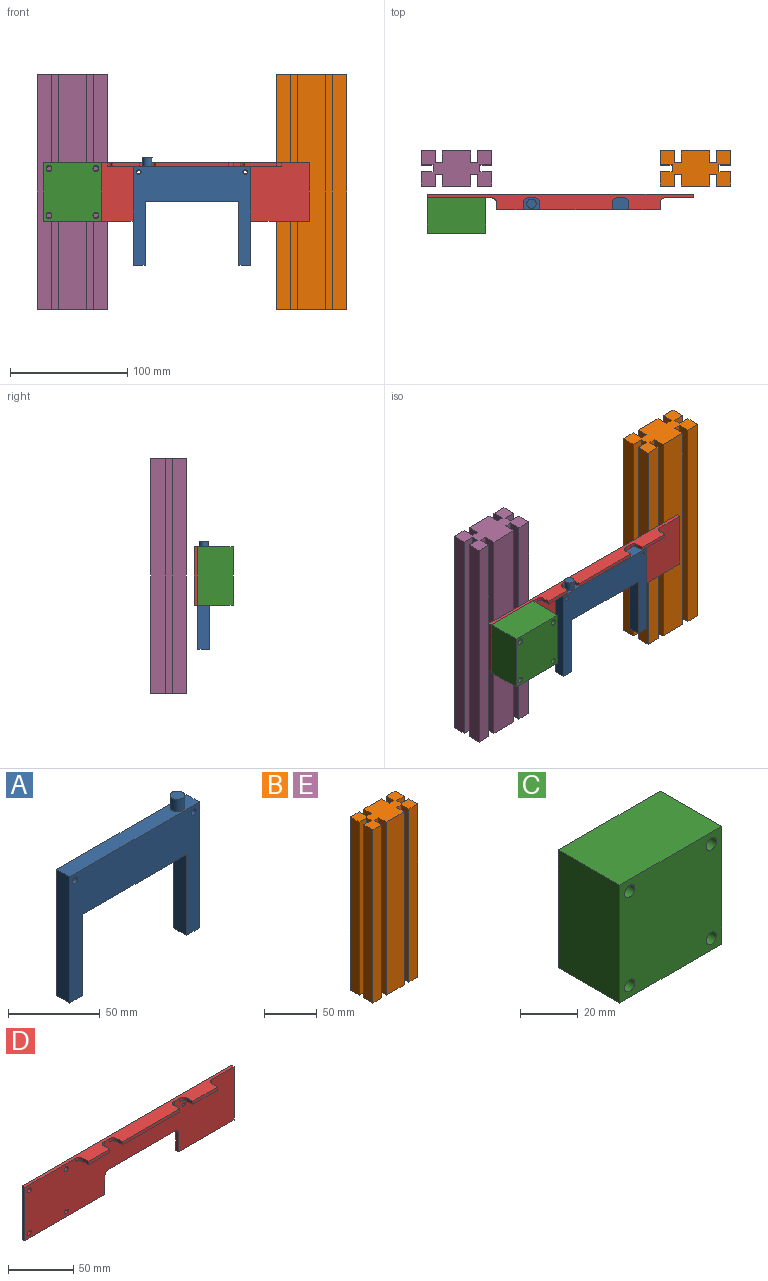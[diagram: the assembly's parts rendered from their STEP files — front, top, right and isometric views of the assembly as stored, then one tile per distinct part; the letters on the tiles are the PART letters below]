
ASSEMBLY  parts=5 mates=3
PART A: 14 faces, bbox 100x10x92 mm
  f0: plane 54x10mm, normal (1,0,0), area 540mm2, adj f1,f7,f8,f9
  f1: plane 80x10mm, normal (0,0,-1), area 800mm2, adj f0,f2,f8,f9
  f2: plane 54x10mm, normal (-1,0,0), area 540mm2, adj f1,f3,f8,f9
  f3: plane 10x10mm, normal (0,0,-1), area 100mm2, adj f2,f4,f8,f9
  f4: plane 84x10mm, normal (1,0,0), area 840mm2, adj f3,f5,f8,f9
  f5: plane 100x10mm, normal (0,0,1), area 949.7mm2, adj f4,f6,f8,f9,f10
  f6: plane 84x10mm, normal (-1,0,0), area 840mm2, adj f5,f7,f8,f9
  f7: plane 10x10mm, normal (0,0,-1), area 100mm2, adj f0,f6,f8,f9
  f8: plane 100x84mm, normal (0,-1,0), area 4054.9mm2, adj f0,f1,f2,f3,f4,f5,f6,f7
  f9: plane 100x84mm, normal (0,1,0), area 4054.9mm2, adj f0,f1,f2,f3,f4,f5,f6,f7
  f10: cylinder r=4mm len=8mm, axis (0,0,-1), area 201.1mm2, adj f5,f11
  f11: plane 8x8mm, normal (0,0,1), area 50.3mm2, adj f10
  f12: cylinder r=2mm len=10mm, axis (0,1,0), area 125.7mm2, adj f8,f9
  f13: cylinder r=2mm len=10mm, axis (0,1,0), area 125.7mm2, adj f8,f9
PART B: 30 faces, bbox 60x30x200 mm
  f0: plane 200x12mm, normal (1,0,0), area 2400mm2, adj f6,f7,f10,f25
  f1: plane 200x12mm, normal (-1,0,0), area 2400mm2, adj f3,f6,f7,f15
  f2: plane 200x24mm, normal (0,1,0), area 4800mm2, adj f6,f7,f12,f28
  f3: plane 200x12mm, normal (0,1,0), area 2400mm2, adj f1,f6,f7,f13
  f4: plane 200x24mm, normal (0,-1,0), area 4800mm2, adj f6,f7,f19,f21
  f5: plane 200x12mm, normal (0,-1,0), area 2400mm2, adj f6,f7,f9,f18
  f6: plane 60x30mm, normal (0,0,1), area 1440mm2, adj f0,f1,f2,f3,f4,f5,f8,f9
  f7: plane 60x30mm, normal (0,0,-1), area 1440mm2, adj f0,f1,f2,f3,f4,f5,f8,f9
  f8: plane 200x12mm, normal (1,0,0), area 2400mm2, adj f6,f7,f11,f24
  f9: plane 200x12mm, normal (-1,0,0), area 2400mm2, adj f5,f6,f7,f16
  f10: plane 200x12mm, normal (0,1,0), area 2400mm2, adj f0,f6,f7,f27
  f11: plane 200x12mm, normal (0,-1,0), area 2400mm2, adj f6,f7,f8,f22
  f12: plane 200x10mm, normal (-1,0,0), area 2000mm2, adj f2,f6,f7,f14
  f13: plane 200x10mm, normal (1,0,0), area 2000mm2, adj f3,f6,f7,f14
  f14: plane 200x6mm, normal (0,1,0), area 1200mm2, adj f6,f7,f12,f13
  f15: plane 200x10mm, normal (0,-1,0), area 2000mm2, adj f1,f6,f7,f17
  f16: plane 200x10mm, normal (0,1,0), area 2000mm2, adj f6,f7,f9,f17
  f17: plane 200x6mm, normal (-1,0,0), area 1200mm2, adj f6,f7,f15,f16
  f18: plane 200x10mm, normal (1,0,0), area 2000mm2, adj f5,f6,f7,f20
  f19: plane 200x10mm, normal (-1,0,0), area 2000mm2, adj f4,f6,f7,f20
  f20: plane 200x6mm, normal (0,-1,0), area 1200mm2, adj f6,f7,f18,f19
  f21: plane 200x10mm, normal (1,0,0), area 2000mm2, adj f4,f6,f7,f23
  f22: plane 200x10mm, normal (-1,0,0), area 2000mm2, adj f6,f7,f11,f23
  f23: plane 200x6mm, normal (0,-1,0), area 1200mm2, adj f6,f7,f21,f22
  f24: plane 200x10mm, normal (0,1,0), area 2000mm2, adj f6,f7,f8,f26
  f25: plane 200x10mm, normal (0,-1,0), area 2000mm2, adj f0,f6,f7,f26
  f26: plane 200x6mm, normal (1,0,0), area 1200mm2, adj f6,f7,f24,f25
  f27: plane 200x10mm, normal (-1,0,0), area 2000mm2, adj f6,f7,f10,f29
  f28: plane 200x10mm, normal (1,0,0), area 2000mm2, adj f2,f6,f7,f29
  f29: plane 200x6mm, normal (0,1,0), area 1200mm2, adj f6,f7,f27,f28
PART C: 10 faces, bbox 50x30x50 mm
  f0: plane 50x30mm, normal (0,0,-1), area 1500mm2, adj f1,f7,f8,f9
  f1: plane 50x30mm, normal (1,0,0), area 1500mm2, adj f0,f2,f8,f9
  f2: plane 50x30mm, normal (0,0,1), area 1500mm2, adj f1,f7,f8,f9
  f3: cylinder r=2.5mm len=30mm, axis (0,1,0), area 471.2mm2, adj f8,f9
  f4: cylinder r=2.5mm len=30mm, axis (0,1,0), area 471.2mm2, adj f8,f9
  f5: cylinder r=2.5mm len=30mm, axis (0,1,0), area 471.2mm2, adj f8,f9
  f6: cylinder r=2.5mm len=30mm, axis (0,1,0), area 471.2mm2, adj f8,f9
  f7: plane 50x30mm, normal (-1,0,0), area 1500mm2, adj f0,f2,f8,f9
  f8: plane 50x50mm, normal (0,-1,0), area 2421.5mm2, adj f0,f1,f2,f3,f4,f5,f6,f7
  f9: plane 50x50mm, normal (0,1,0), area 2421.5mm2, adj f0,f1,f2,f3,f4,f5,f6,f7
PART D: 36 faces, bbox 227x13x50 mm
  f0: plane 227x50mm, normal (0,-1,0), area 9156.3mm2, adj f1,f3,f4,f5,f6,f7,f8,f9
  f1: plane 60x3mm, normal (0,0,-1), area 180mm2, adj f0,f2,f5,f14
  f2: plane 227x50mm, normal (0,1,0), area 9564.3mm2, adj f1,f3,f4,f5,f6,f7,f8,f9
  f3: plane 50x3mm, normal (-1,0,0), area 150mm2, adj f0,f2,f4,f6
  f4: plane 87x3mm, normal (0,0,-1), area 261mm2, adj f0,f2,f3,f13
  f5: plane 50x3mm, normal (1,0,0), area 150mm2, adj f0,f1,f2,f6
  f6: plane 227x13mm, normal (0,0,1), area 1821.6mm2, adj f0,f2,f3,f5,f18,f20,f21,f22
  f7: cylinder r=2.1mm len=4.2mm, axis (0,-1,0), area 39.6mm2, adj f0,f2
  f8: cylinder r=2.1mm len=4.2mm, axis (0,-1,0), area 39.6mm2, adj f0,f2
  f9: cylinder r=2.1mm len=4.2mm, axis (0,-1,0), area 39.6mm2, adj f0,f2
  f10: cylinder r=2.1mm len=4.2mm, axis (0,-1,0), area 39.6mm2, adj f0,f2
  f11: cylinder r=1.65mm len=3.3mm, axis (0,-1,0), area 31.1mm2, adj f0,f2
  f12: cylinder r=1.65mm len=3.3mm, axis (0,-1,0), area 31.1mm2, adj f0,f2
  f13: plane 17.5x3mm, normal (1,0,0), area 52.5mm2, adj f0,f2,f4,f16
  f14: plane 17.5x3mm, normal (-1,0,0), area 52.5mm2, adj f0,f1,f2,f17
  f15: plane 72x3mm, normal (0,0,-1), area 216mm2, adj f0,f2,f16,f17
  f16: cylinder r=4mm len=4mm, axis (0,1,0), area 18.8mm2, adj f0,f2,f13,f15
  f17: cylinder r=4mm len=4mm, axis (0,1,0), area 18.8mm2, adj f0,f2,f14,f15
  f18: plane 6x3mm, normal (-1,0,0), area 18mm2, adj f6,f19,f21,f34
  f19: plane 31x10mm, normal (0,0,-1), area 236.9mm2, adj f0,f18,f20,f21,f34,f35
  f20: plane 6x3mm, normal (1,0,0), area 18mm2, adj f6,f19,f21,f35
  f21: plane 23x3mm, normal (0,-1,0), area 69mm2, adj f6,f18,f19,f20
  f22: plane 6x3mm, normal (-1,0,0), area 18mm2, adj f6,f23,f25,f32
  f23: plane 70x10mm, normal (0,0,-1), area 626.9mm2, adj f0,f22,f24,f25,f32,f33
  f24: plane 6x3mm, normal (1,0,0), area 18mm2, adj f6,f23,f25,f33
  f25: plane 62x3mm, normal (0,-1,0), area 186mm2, adj f6,f22,f23,f24
  f26: plane 6x3mm, normal (-1,0,0), area 18mm2, adj f6,f27,f29,f30
  f27: plane 35x10mm, normal (0,0,-1), area 276.9mm2, adj f0,f26,f28,f29,f30,f31
  f28: plane 6x3mm, normal (1,0,0), area 18mm2, adj f6,f27,f29,f31
  f29: plane 27x3mm, normal (0,-1,0), area 81mm2, adj f6,f26,f27,f28
  f30: cylinder r=4mm len=4mm, axis (0,0,-1), area 18.8mm2, adj f0,f6,f26,f27
  f31: cylinder r=4mm len=4mm, axis (0,0,1), area 18.8mm2, adj f0,f6,f27,f28
  f32: cylinder r=4mm len=4mm, axis (0,0,-1), area 18.8mm2, adj f0,f6,f22,f23
  f33: cylinder r=4mm len=4mm, axis (0,0,1), area 18.8mm2, adj f0,f6,f23,f24
  f34: cylinder r=4mm len=4mm, axis (0,0,-1), area 18.8mm2, adj f0,f6,f18,f19
  f35: cylinder r=4mm len=4mm, axis (0,0,1), area 18.8mm2, adj f0,f6,f19,f20
PART E: same geometry as B
PLACE A rot(axis=(0,0,1),180deg) t=(166.42,-5.06,-14.75)mm
PLACE B t=(228.42,4.94,-6.25)mm
PLACE C t=(24.42,4.94,-6.25)mm
PLACE D t=(-0.58,7.94,-31.25)mm
PLACE E t=(24.42,4.94,-6.25)mm
MATE fastened A.f13 <-> D.f11  axis (0,1,0) through (80.92,4.94,10.75)mm
MATE fastened D.f7 <-> C.f3  axis (0,-1,0) through (4.42,4.94,13.75)mm
MATE fastened B.f6 <-> E.f6  axis (0,0,1) through (228.42,29.94,93.75)mm
